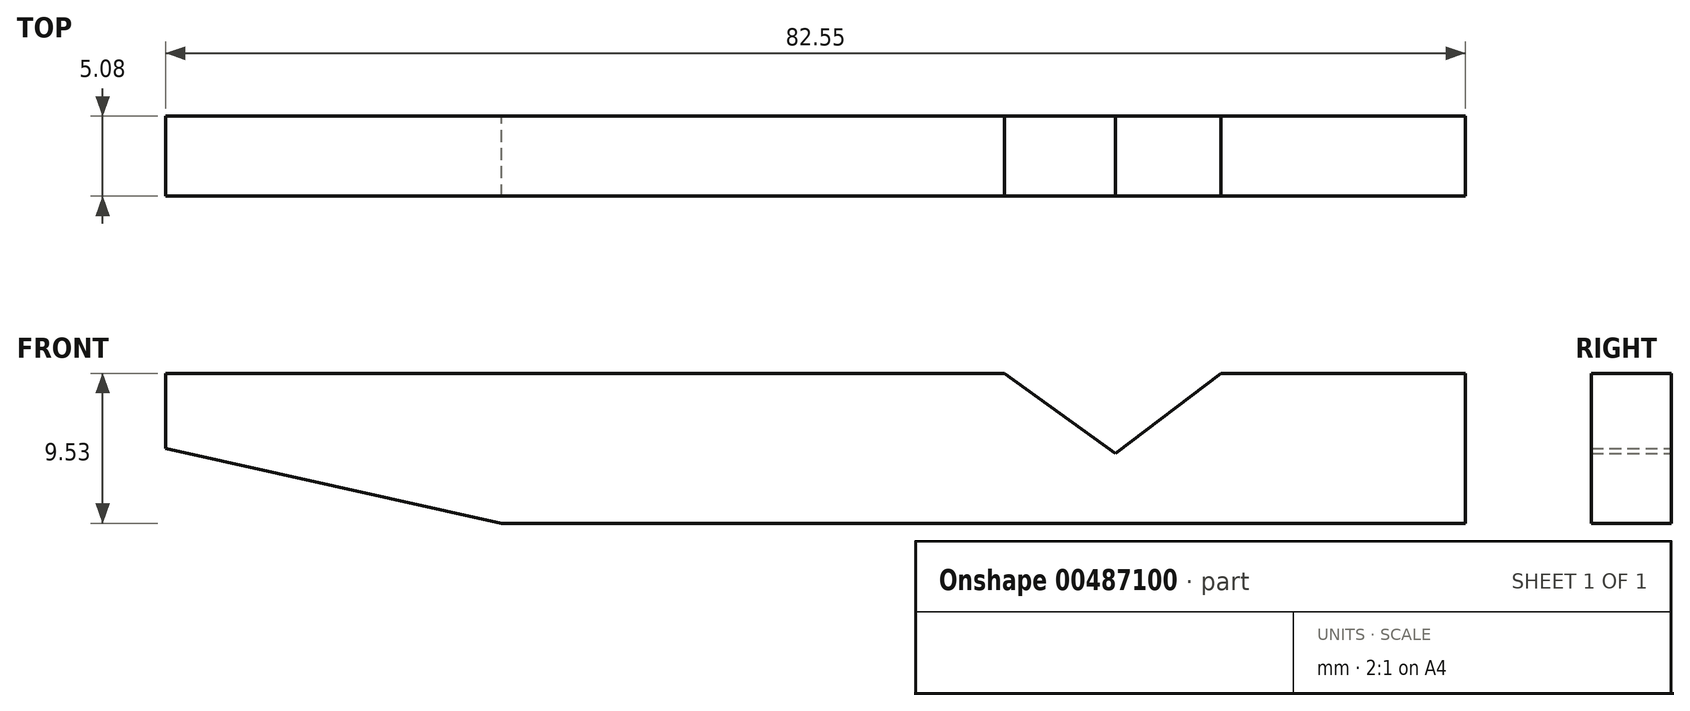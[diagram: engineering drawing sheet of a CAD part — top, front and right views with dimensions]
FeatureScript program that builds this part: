
annotation { "Feature Type Name" : "Feature", "Feature Type Description" : "" }
export const myFeature = defineFeature(function(context is Context, id is Id, definition is map)
    precondition{}
    {
        {
            var Q0;
            Q0=qCreatedBy(makeId("Front.planeOp"),FACE);
            var sketch = newSketch(context, id + "F0", { "sketchPlane" : qUnion([Q0])});
            skLineSegment(sketch, "E0.bottom", {"start": v(-28.81, -30.48) * mm, "end": v(24.48, -30.48) * mm});
            skLineSegment(sketch, "E0.top", {"start": v(-7.46, -40) * mm, "end": v(53.74, -40) * mm});
            skLineSegment(sketch, "E0.left", {"start": v(-28.81, -30.48) * mm, "end": v(-28.81, -35.24) * mm});
            skLineSegment(sketch, "E0.right", {"start": v(53.74, -30.48) * mm, "end": v(53.74, -40) * mm});
            skLineSegment(sketch, "E1", {"start": v(53.74, -30.48) * mm, "end": v(38.21, -30.48) * mm});
            skLineSegment(sketch, "E2", {"start": v(31.51, -35.56) * mm, "end": v(24.48, -30.48) * mm});
            skLineSegment(sketch, "E3", {"start": v(31.51, -35.56) * mm, "end": v(38.21, -30.48) * mm});
            skLineSegment(sketch, "E4.trimOffspring", {"start": v(38.21, -30.48) * mm, "end": v(53.74, -30.48) * mm});
            skLineSegment(sketch, "E5", {"start": v(-28.81, -35.24) * mm, "end": v(-7.46, -40) * mm});
            skPoint(sketch, "E6.orphan", {"position": v(-28.81, -40) * mm});
            skSolve(sketch);
        }
        {
            var Q0;
            Q0 = qSketchRegion(id + "F0", true);
            extrude(context, id + "F1", {"entities" : qUnion([Q0]), "depth" : 5.08 * mm});
        }
    });
